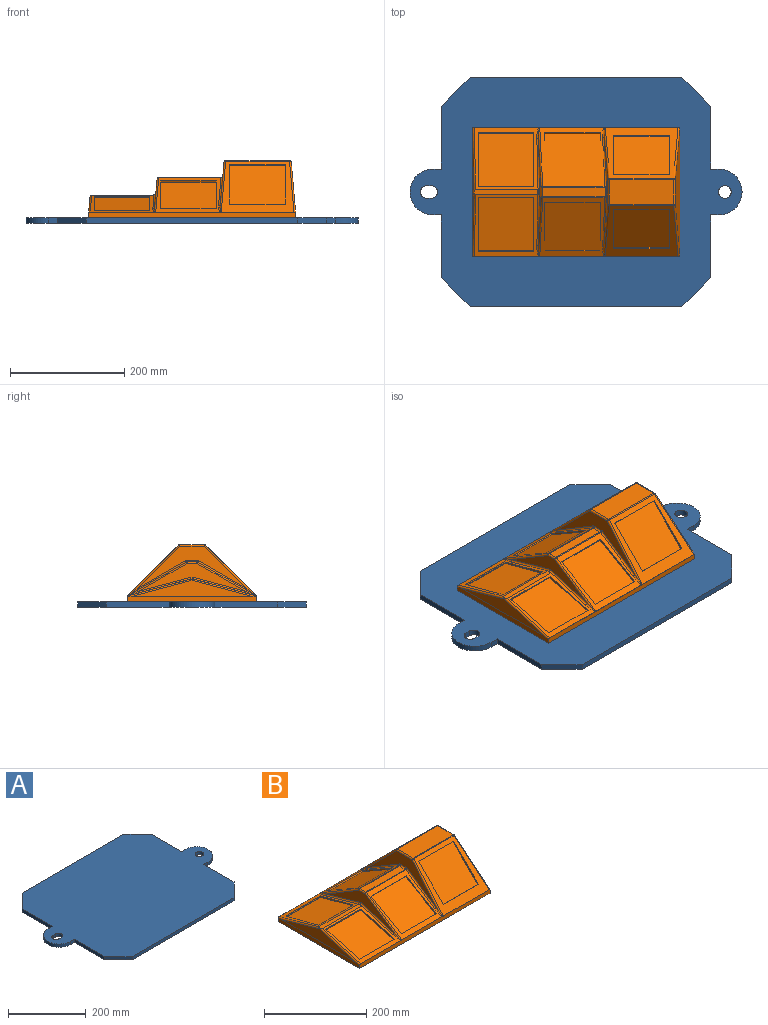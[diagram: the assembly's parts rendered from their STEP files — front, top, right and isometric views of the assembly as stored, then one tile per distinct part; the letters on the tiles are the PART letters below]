
ASSEMBLY  parts=2 mates=1
PART A: 23 faces, bbox 580x400x10 mm
  f0: plane 110x10mm, normal (-1,0,0), area 1100mm2, adj f6,f7,f10,f16
  f1: plane 110x10mm, normal (1,0,0), area 1100mm2, adj f6,f7,f11,f12
  f2: plane 110x10mm, normal (-1,0,0), area 1100mm2, adj f6,f7,f8,f22
  f3: plane 370x10mm, normal (0,-1,0), area 3700mm2, adj f6,f7,f10,f11
  f4: plane 110x10mm, normal (1,0,0), area 1100mm2, adj f6,f7,f9,f13
  f5: plane 370x10mm, normal (0,1,0), area 3700mm2, adj f6,f7,f8,f9
  f6: plane 580x400mm, normal (0,0,1), area 189490.3mm2, adj f0,f1,f2,f3,f4,f5,f8,f9
  f7: plane 580x400mm, normal (0,0,-1), area 189490.3mm2, adj f0,f1,f2,f3,f4,f5,f8,f9
  f8: plane 50x50mm, normal (-0.71,0.71,0), area 707.1mm2, adj f2,f5,f6,f7
  f9: plane 50x50mm, normal (0.71,0.71,0), area 707.1mm2, adj f4,f5,f6,f7
  f10: plane 50x50mm, normal (-0.71,-0.71,0), area 707.1mm2, adj f0,f3,f6,f7
  f11: plane 50x50mm, normal (0.71,-0.71,0), area 707.1mm2, adj f1,f3,f6,f7
  f12: plane 15x10mm, normal (0,-1,0), area 150mm2, adj f1,f6,f7,f14
  f13: plane 15x10mm, normal (0,1,0), area 150mm2, adj f4,f6,f7,f14
  f14: cylinder r=40mm len=80mm, axis (0,0,-1), area 1256.6mm2, adj f6,f7,f12,f13
  f15: cylinder r=11mm len=22mm, axis (0,0,-1), area 691.2mm2, adj f6,f7
  f16: plane 15x10mm, normal (0,-1,0), area 150mm2, adj f0,f6,f7,f17
  f17: cylinder r=40mm len=80mm, axis (0,0,-1), area 1256.6mm2, adj f6,f7,f16,f22
  f18: plane 10x8mm, normal (0,1,0), area 80mm2, adj f6,f7,f19,f21
  f19: cylinder r=11mm len=22mm, axis (0,0,-1), area 345.6mm2, adj f6,f7,f18,f20
  f20: plane 10x8mm, normal (0,-1,0), area 80mm2, adj f6,f7,f19,f21
  f21: cylinder r=11mm len=22mm, axis (0,0,-1), area 345.6mm2, adj f6,f7,f18,f20
  f22: plane 15x10mm, normal (0,1,0), area 150mm2, adj f2,f6,f7,f17
PART B: 97 faces, bbox 362.2x228.8x100.1 mm
  f0: plane 116.89x113.01mm, normal (0,0.26,0.97), area 2815.5mm2, adj f1,f9,f15,f27,f28,f29,f31,f36
  f1: plane 351x0.02mm, normal (0,0,-1), area 4.7mm2, adj f0,f2,f7,f8,f10,f16,f95
  f2: plane 127.99x89.23mm, normal (0,0.71,0.71), area 5627mm2, adj f1,f7,f12,f14,f16,f17,f18,f19
  f3: plane 192.03x74.25mm, normal (-1,0,0.09), area 3492.7mm2, adj f66,f72,f73,f83,f85,f87,f88,f89
  f4: plane 218.06x87.26mm, normal (1,0,0.09), area 11457.6mm2, adj f34,f65,f70,f71
  f5: plane 186.94x49.18mm, normal (-1,0,0.09), area 2673.6mm2, adj f77,f80,f81,f92,f93
  f6: plane 204.8x27.44mm, normal (-1,0,0.09), area 2820.3mm2, adj f33,f95,f96
  f7: plane 0.01x0.01mm, normal (1,0,0), area 0mm2, adj f1,f2,f16
  f8: plane 0.01x0mm, normal (-1,0,0), area 0mm2, adj f1,f16,f95
  f9: plane 0.01x0.01mm, normal (-1,0,0), area 0mm2, adj f0,f10,f15
  f10: plane 120.4x103.35mm, normal (0,0.5,0.87), area 3584.5mm2, adj f1,f9,f12,f14,f15,f22,f23,f24
  f11: plane 108.88x16.57mm, normal (0,0,1), area 1804.4mm2, adj f81,f82,f86,f87
  f12: plane 0.01x0.01mm, normal (-1,0,0), area 0mm2, adj f2,f10,f14
  f13: plane 111.5x43.54mm, normal (0,0,1), area 4854.9mm2, adj f67,f70,f73,f76
  f14: plane 6.14x0.02mm, normal (0,1,0), area 0mm2, adj f2,f10,f12,f79
  f15: plane 3.56x0.01mm, normal (0,1,0), area 0mm2, adj f0,f9,f10,f91
  f16: plane 361.52x10.01mm, normal (0,1,0), area 3611.9mm2, adj f1,f2,f7,f8,f32,f33,f34,f65
  f17: plane 97x2.12mm, normal (0,-0.71,0.71), area 291mm2, adj f2,f18,f20,f21
  f18: plane 70.71x70.71mm, normal (1,0,0), area 291mm2, adj f2,f17,f19,f21
  f19: plane 97x2.12mm, normal (0,0.71,-0.71), area 291mm2, adj f2,f18,f20,f21
  f20: plane 70.71x70.71mm, normal (-1,0,0), area 291mm2, adj f2,f17,f19,f21
  f21: plane 97x68.59mm, normal (0,0.71,0.71), area 9409mm2, adj f17,f18,f19,f20
  f22: plane 85.5x51.1mm, normal (1,0,0), area 291mm2, adj f10,f23,f25,f26
  f23: plane 97x2.6mm, normal (0,0.87,-0.5), area 291mm2, adj f10,f22,f24,f26
  f24: plane 85.5x51.1mm, normal (-1,0,0), area 291mm2, adj f10,f23,f25,f26
  f25: plane 97x2.6mm, normal (0,-0.87,0.5), area 291mm2, adj f10,f22,f24,f26
  f26: plane 97x84mm, normal (0,0.5,0.87), area 9409mm2, adj f22,f23,f24,f25
  f27: plane 97x2.59mm, normal (0,-0.97,0.26), area 260.1mm2, adj f0,f28,f29,f35
  f28: plane 94.47x27.7mm, normal (1,0,0), area 290.8mm2, adj f0,f27,f30,f31,f35
  f29: plane 94.47x27.7mm, normal (-1,0,0), area 290.8mm2, adj f0,f27,f30,f31,f35
  f30: plane 97x92.55mm, normal (0,0.26,0.97), area 9293.6mm2, adj f28,f29,f31,f35
  f31: plane 97x2.9mm, normal (0,0.97,-0.26), area 291mm2, adj f0,f28,f29,f30
  f32: plane 361.52x226mm, normal (0,0,-1), area 81704.3mm2, adj f16,f33,f34,f46
  f33: plane 226x10mm, normal (-1,0,0), area 2242.7mm2, adj f6,f16,f32,f46,f95,f96
  f34: plane 226x10mm, normal (1,0,0), area 2251.7mm2, adj f4,f16,f32,f46,f65,f71
  f35: plane 97x1.23mm, normal (0,0,1), area 119.4mm2, adj f27,f28,f29,f30
  f36: plane 116.89x113.01mm, normal (0,-0.26,0.97), area 2815.5mm2, adj f0,f37,f41,f45,f57,f58,f59,f61
  f37: plane 351x0.02mm, normal (0,0,-1), area 4.7mm2, adj f36,f38,f39,f40,f42,f46,f96
  f38: plane 127.99x89.23mm, normal (0,-0.71,0.71), area 5627mm2, adj f37,f39,f43,f44,f46,f47,f48,f49
  f39: plane 0.01x0.01mm, normal (1,0,0), area 0mm2, adj f37,f38,f46
  f40: plane 0.01x0mm, normal (-1,0,0), area 0mm2, adj f37,f46,f96
  f41: plane 0.01x0.01mm, normal (-1,0,0), area 0mm2, adj f36,f42,f45
  f42: plane 120.4x103.35mm, normal (0,-0.5,0.87), area 3584.5mm2, adj f37,f41,f43,f44,f45,f52,f53,f54
  f43: plane 0.01x0.01mm, normal (-1,0,0), area 0mm2, adj f38,f42,f44
  f44: plane 6.14x0.02mm, normal (0,-1,0), area 0mm2, adj f38,f42,f43,f90
  f45: plane 3.56x0.01mm, normal (0,-1,0), area 0mm2, adj f36,f41,f42,f94
  f46: plane 361.52x10.01mm, normal (0,-1,0), area 3611.9mm2, adj f32,f33,f34,f37,f38,f39,f40,f71
  f47: plane 97x2.12mm, normal (0,0.71,0.71), area 291mm2, adj f38,f48,f50,f51
  f48: plane 70.71x70.71mm, normal (1,0,0), area 291mm2, adj f38,f47,f49,f51
  f49: plane 97x2.12mm, normal (0,-0.71,-0.71), area 291mm2, adj f38,f48,f50,f51
  f50: plane 70.71x70.71mm, normal (-1,0,0), area 291mm2, adj f38,f47,f49,f51
  f51: plane 97x68.59mm, normal (0,-0.71,0.71), area 9409mm2, adj f47,f48,f49,f50
  f52: plane 85.5x51.1mm, normal (1,0,0), area 291mm2, adj f42,f53,f55,f56
  f53: plane 97x2.6mm, normal (0,-0.87,-0.5), area 291mm2, adj f42,f52,f54,f56
  f54: plane 85.5x51.1mm, normal (-1,0,0), area 291mm2, adj f42,f53,f55,f56
  f55: plane 97x2.6mm, normal (0,0.87,0.5), area 291mm2, adj f42,f52,f54,f56
  f56: plane 97x84mm, normal (0,-0.5,0.87), area 9409mm2, adj f52,f53,f54,f55
  f57: plane 97x2.59mm, normal (0,0.97,0.26), area 260.1mm2, adj f36,f58,f59,f62
  f58: plane 94.47x27.7mm, normal (1,0,0), area 290.8mm2, adj f36,f57,f60,f61,f62
  f59: plane 94.47x27.7mm, normal (-1,0,0), area 290.8mm2, adj f36,f57,f60,f61,f62
  f60: plane 97x92.55mm, normal (0,-0.26,0.97), area 9293.6mm2, adj f58,f59,f61,f62
  f61: plane 97x2.9mm, normal (0,-0.97,-0.26), area 291mm2, adj f36,f58,f59,f60
  f62: plane 97x1.23mm, normal (0,0,1), area 119.4mm2, adj f57,f58,f59,f60
  f63: plane 111.03x9.57mm, normal (0,0,1), area 1055.8mm2, adj f0,f36,f64,f95,f96
  f64: plane 9.57x1.28mm, normal (-1,0,0), area 6.1mm2, adj f0,f36,f63
  f65: cylinder r=3mm len=92.57mm, axis (0.06,0.71,-0.71), area 572.9mm2, adj f2,f4,f16,f34,f68
  f66: cylinder r=3mm len=90.97mm, axis (0.06,-0.71,0.71), area 536.6mm2, adj f2,f3,f69,f79
  f67: cylinder r=3mm len=111.5mm, axis (1,0,0), area 262.7mm2, adj f2,f13,f68,f69
  f68: sphere r=3mm, area 6.5mm2, adj f65,f67,f70
  f69: sphere r=3mm, area 6.5mm2, adj f66,f67,f73
  f70: cylinder r=3mm len=43.54mm, axis (0,1,0), area 193.8mm2, adj f4,f13,f68,f74
  f71: cylinder r=3mm len=92.57mm, axis (0.06,-0.71,-0.71), area 572.9mm2, adj f4,f34,f38,f46,f74
  f72: cylinder r=3mm len=90.97mm, axis (0.06,0.71,0.71), area 536.6mm2, adj f3,f38,f75,f90
  f73: cylinder r=3mm len=43.54mm, axis (0,-1,0), area 193.8mm2, adj f3,f13,f69,f75
  f74: sphere r=3mm, area 6.5mm2, adj f70,f71,f76
  f75: sphere r=3mm, area 6.5mm2, adj f72,f73,f76
  f76: cylinder r=3mm len=111.5mm, axis (1,0,0), area 262.7mm2, adj f13,f38,f74,f75
  f77: cylinder r=3mm len=104.39mm, axis (0.04,-0.87,0.5), area 500.7mm2, adj f5,f10,f78,f91
  f78: sphere r=3mm, area 4.3mm2, adj f77,f81,f82
  f79: bspline ~22.43x15.67mm, area 63.1mm2, adj f2,f10,f14,f66,f83
  f80: cylinder r=3mm len=104.39mm, axis (0.04,0.87,0.5), area 500.7mm2, adj f5,f42,f84,f94
  f81: cylinder r=3mm len=16.57mm, axis (0,-1,0), area 73.8mm2, adj f5,f11,f78,f84
  f82: cylinder r=3mm len=108.88mm, axis (1,0,0), area 171mm2, adj f10,f11,f78,f85
  f83: cylinder r=3mm len=86.23mm, axis (-0.04,0.87,-0.5), area 439.3mm2, adj f3,f10,f79,f85
  f84: sphere r=3mm, area 4.3mm2, adj f80,f81,f86
  f85: bspline ~3.86x3.54mm, area 9.7mm2, adj f3,f82,f83,f87
  f86: cylinder r=3mm len=108.88mm, axis (1,0,0), area 171mm2, adj f11,f42,f84,f88
  f87: cylinder r=3mm len=16.57mm, axis (0,1,0), area 73.8mm2, adj f3,f11,f85,f88
  f88: bspline ~3.86x3.54mm, area 9.7mm2, adj f3,f86,f87,f89
  f89: cylinder r=3mm len=86.23mm, axis (-0.04,-0.87,-0.5), area 439.3mm2, adj f3,f42,f88,f90
  f90: bspline ~22.43x15.67mm, area 63.1mm2, adj f38,f42,f44,f72,f89
  f91: bspline ~21.85x8.62mm, area 62.1mm2, adj f0,f10,f15,f77,f92
  f92: cylinder r=3mm len=94.25mm, axis (-0.02,0.97,-0.26), area 429.9mm2, adj f0,f5,f91,f93
  f93: cylinder r=3mm len=94.25mm, axis (-0.02,-0.97,-0.26), area 429.9mm2, adj f5,f36,f92,f94
  f94: bspline ~21.85x8.62mm, area 62.1mm2, adj f36,f42,f45,f80,f93
  f95: cylinder r=3mm len=113.93mm, axis (0.02,-0.97,0.26), area 506.1mm2, adj f0,f1,f6,f8,f16,f33,f63,f96
  f96: cylinder r=3mm len=113.93mm, axis (0.02,0.97,0.26), area 506.1mm2, adj f6,f33,f36,f37,f40,f46,f63,f95
PLACE A t=(14.26,16.44,48.6)mm
PLACE B t=(71.38,216.44,68.6)mm
MATE planar A.f6 <-> B.f32  axis (0,0,1) through (249.49,216.44,58.6)mm
